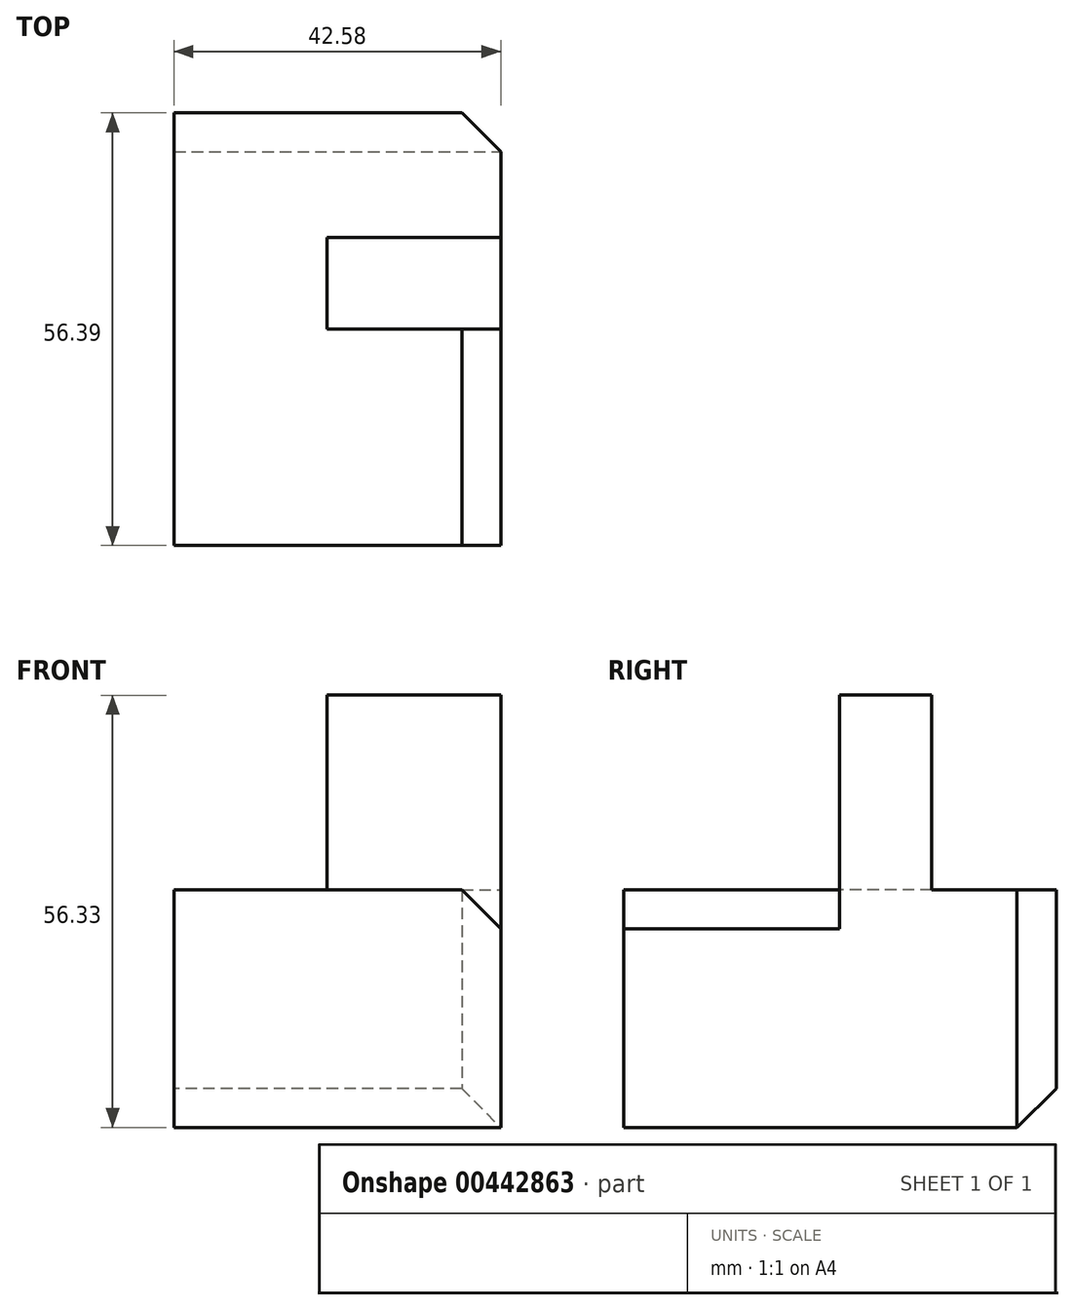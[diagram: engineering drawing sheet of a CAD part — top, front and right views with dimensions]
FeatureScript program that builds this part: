
annotation { "Feature Type Name" : "Feature", "Feature Type Description" : "" }
export const myFeature = defineFeature(function(context is Context, id is Id, definition is map)
    precondition{}
    {
        {
            var Q0;
            Q0=qCreatedBy(makeId("Front.planeOp"),FACE);
            var sketch = newSketch(context, id + "F0", { "sketchPlane" : qUnion([Q0])});
            skLineSegment(sketch, "E0.bottom", {"start": v(0, 0) * mm, "end": v(42.58, 0) * mm});
            skLineSegment(sketch, "E0.top", {"start": v(0, 30.93) * mm, "end": v(42.58, 30.93) * mm});
            skLineSegment(sketch, "E0.left", {"start": v(0, 0) * mm, "end": v(0, 30.93) * mm});
            skLineSegment(sketch, "E0.right", {"start": v(42.58, 0) * mm, "end": v(42.58, 30.93) * mm});
            skSolve(sketch);
        }
        {
            var Q0;
            Q0=makeQuery(id+"F0.imprint","IMPRINT",FACE,{"disambiguationData":[TD([[makeQuery(id+"F0.imprint","IMPRINT",EDGE,{"derivedFrom":sQuery(id+"F0.wireOp",EDGE,"E0.bottom")}),1.0]])]});
            extrude(context, id + "F1", {"entities" : qUnion([Q0]), "depth" : 56.4 * mm});
        }
        {
            var Q0;
            Q0=makeQuery(id+"F1.opExtrude","SWEPT_FACE",FACE,{"disambiguationData":[OSD([sQuery(id+"F0.wireOp",EDGE,"E0.top")])]});
            var sketch = newSketch(context, id + "F2", { "sketchPlane" : qUnion([Q0])});
            skLineSegment(sketch, "E1.bottom", {"start": v(19.94, -16.2) * mm, "end": v(42.58, -16.2) * mm});
            skLineSegment(sketch, "E1.top", {"start": v(19.94, -28.2) * mm, "end": v(42.58, -28.2) * mm});
            skLineSegment(sketch, "E1.left", {"start": v(19.94, -16.2) * mm, "end": v(19.94, -28.2) * mm});
            skLineSegment(sketch, "E1.right", {"start": v(42.58, -16.2) * mm, "end": v(42.58, -28.2) * mm});
            skSolve(sketch);
        }
        {
            var Q0;
            Q0=makeQuery(id+"F2.imprint","IMPRINT",FACE,{"disambiguationData":[TD([[makeQuery(id+"F2.imprint","IMPRINT",EDGE,{"derivedFrom":sQuery(id+"F2.wireOp",EDGE,"E1.bottom")}),-1.0]])]});
            extrude(context, id + "F3", {"entities" : qUnion([Q0]), "operationType" : NewBodyOperationType.ADD, "depth" : 25.4 * mm});
        }
        {
            var Q0;
            Q0=makeQuery(id+"F3.opExtrude","CAP_EDGE",EDGE,{"disambiguationData":[OSD([sQuery(id+"F2.wireOp",EDGE,"E1.top")])],"isStart":true});
            var Q1;
            {var subQ0=sQuery(id+"F0.wireOp",EDGE,"E0.right");var subQ1=sQuery(id+"F0.wireOp",EDGE,"E0.top");Q1=makeQuery(id+"F3.boolean.opBoolean","SPLIT",EDGE,{"disambiguationData":[TD([makeQuery(id+"F3.opExtrude","SWEPT_FACE",FACE,{"disambiguationData":[OSD([sQuery(id+"F2.wireOp",EDGE,"E1.top")])]})])],"derivedFrom":makeQuery(id+"F1.opExtrude","SWEPT_EDGE",EDGE,{"disambiguationData":[OSD([subQ1,subQ0])]})});}
            var Q2;
            Q2=makeQuery(id+"F1.opExtrude","CAP_EDGE",EDGE,{"disambiguationData":[OSD([sQuery(id+"F0.wireOp",EDGE,"E0.bottom")])],"isStart":true});
            var Q3;
            Q3=makeQuery(id+"F1.opExtrude","CAP_EDGE",EDGE,{"disambiguationData":[OSD([sQuery(id+"F0.wireOp",EDGE,"E0.right")])],"isStart":true});
            chamfer(context, id + "F4", {"entities" : qUnion([Q0, Q1, Q2, Q3]), "width" : 5.08 * mm, "tangentPropagation" : true});
        }
    });
